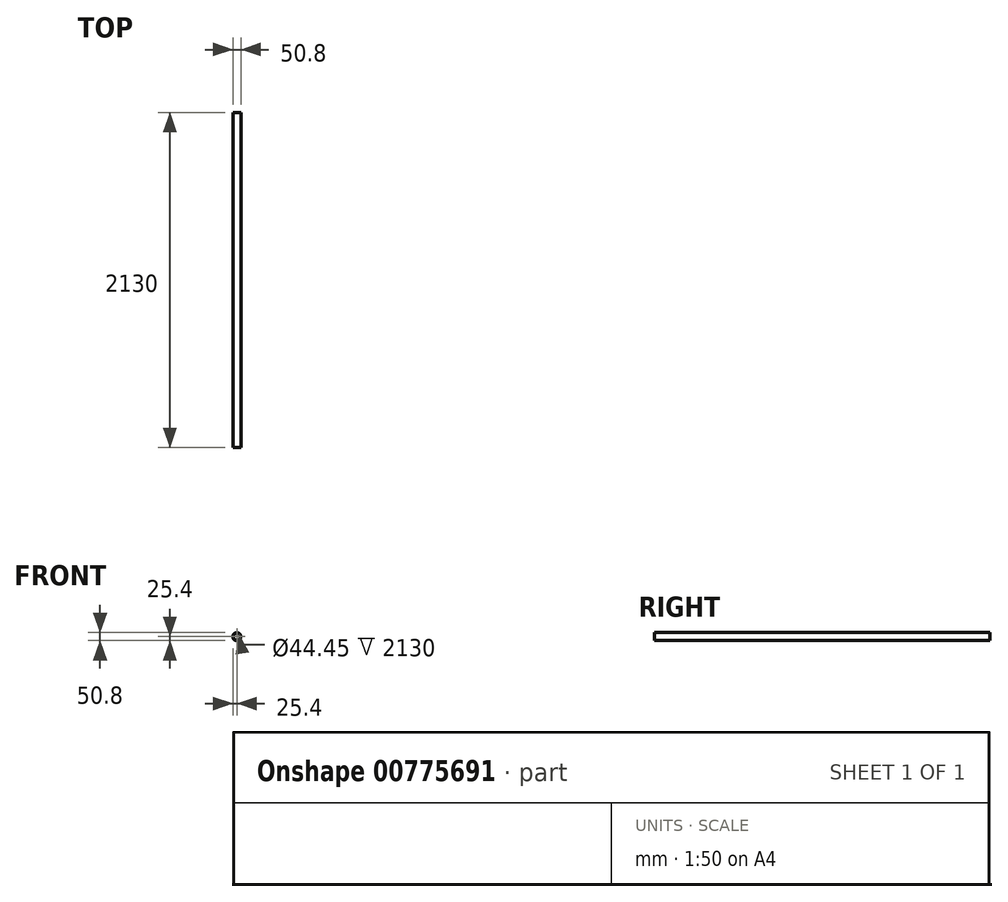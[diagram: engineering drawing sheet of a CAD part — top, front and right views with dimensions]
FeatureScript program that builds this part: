
annotation { "Feature Type Name" : "Feature", "Feature Type Description" : "" }
export const myFeature = defineFeature(function(context is Context, id is Id, definition is map)
    precondition{}
    {
        {
            var Q0;
            Q0=qCreatedBy(makeId("Front.planeOp"),FACE);
            var sketch = newSketch(context, id + "F0", { "sketchPlane" : qUnion([Q0])});
            skCircle(sketch, "E0", {"center": v(0, 0) * mm, "radius": 22.23 * mm});
            skCircle(sketch, "E1", {"center": v(0, 0) * mm, "radius": 25.4 * mm});
            skSolve(sketch);
        }
        {
            var Q0;
            Q0=makeQuery(id+"F0.imprint","IMPRINT",FACE,{"disambiguationData":[TD([[makeQuery(id+"F0.imprint","IMPRINT",EDGE,{"derivedFrom":sQuery(id+"F0.wireOp",EDGE,"E0")}),-1.0]])]});
            extrude(context, id + "F1", {"entities" : qUnion([Q0]), "depth" : 2130 * mm, "offsetDistance" : 25 * mm, "symmetric" : true});
        }
    });
